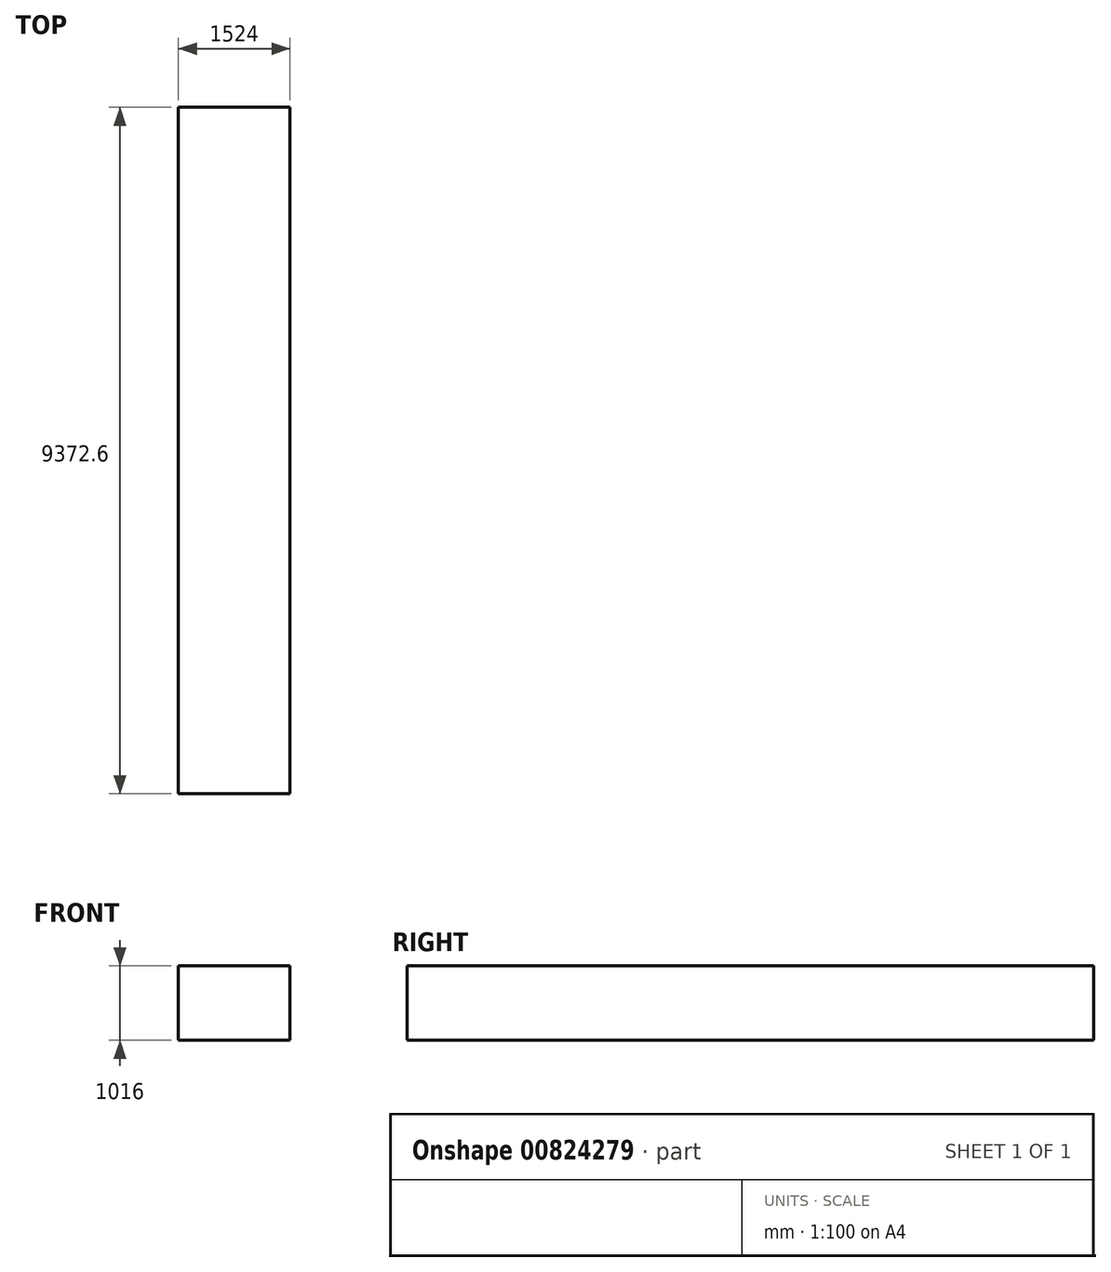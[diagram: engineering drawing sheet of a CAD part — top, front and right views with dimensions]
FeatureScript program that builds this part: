
annotation { "Feature Type Name" : "Feature", "Feature Type Description" : "" }
export const myFeature = defineFeature(function(context is Context, id is Id, definition is map)
    precondition{}
    {
        {
            var Q0;
            Q0=qCreatedBy(makeId("Front.planeOp"),FACE);
            var sketch = newSketch(context, id + "F0", { "sketchPlane" : qUnion([Q0])});
            skLineSegment(sketch, "E0.bottom", {"start": v(-762, 508) * mm, "end": v(762, 508) * mm});
            skLineSegment(sketch, "E0.top", {"start": v(-762, -508) * mm, "end": v(762, -508) * mm});
            skLineSegment(sketch, "E0.left", {"start": v(-762, 508) * mm, "end": v(-762, -508) * mm});
            skLineSegment(sketch, "E0.right", {"start": v(762, 508) * mm, "end": v(762, -508) * mm});
            skSolve(sketch);
        }
        {
            var Q0;
            Q0 = qSketchRegion(id + "F0", true);
            extrude(context, id + "F1", {"entities" : qUnion([Q0]), "depth" : 9372.6 * mm, "offsetDistance" : 25.4 * mm, "symmetric" : true});
        }
    });
